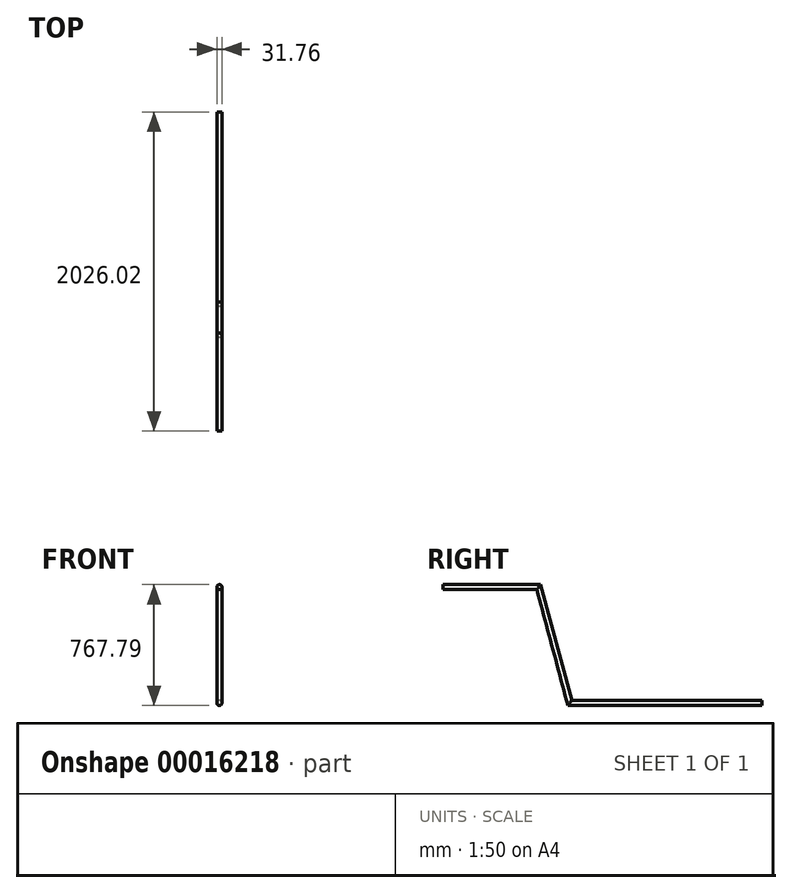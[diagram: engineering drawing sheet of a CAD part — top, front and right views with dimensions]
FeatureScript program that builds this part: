
annotation { "Feature Type Name" : "Feature", "Feature Type Description" : "" }
export const myFeature = defineFeature(function(context is Context, id is Id, definition is map)
    precondition{}
    {
        {
            var Q0;
            Q0=qCreatedBy(makeId("Right.planeOp"),FACE);
            var sketch = newSketch(context, id + "F0", { "sketchPlane" : qUnion([Q0])});
            skLineSegment(sketch, "E0", {"start": v(0, 0) * mm, "end": v(-1219.2, 0) * mm});
            skLineSegment(sketch, "E1", {"start": v(-1219.2, 0) * mm, "end": v(-1416.42, 736.04) * mm});
            skLineSegment(sketch, "E2", {"start": v(-1416.42, 736.04) * mm, "end": v(-2026.02, 736.04) * mm});
            skLineSegment(sketch, "E3", {"start": v(0, 0) * mm, "end": v(-2540, 0) * mm, "construction": true});
            skSolve(sketch);
        }
        {
            var Q0;
            Q0=qCreatedBy(makeId("Front.planeOp"),FACE);
            var sketch = newSketch(context, id + "F1", { "sketchPlane" : qUnion([Q0])});
            skCircle(sketch, "E4", {"center": v(0, 0) * mm, "radius": 15.88 * mm});
            skSolve(sketch);
        }
        {
            var Q0;
            Q0=makeQuery(id+"F1.imprint","IMPRINT",FACE,{"disambiguationData":[TD([[makeQuery(id+"F1.imprint","IMPRINT",EDGE,{"derivedFrom":sQuery(id+"F1.wireOp",EDGE,"E4")}),1.0]])]});
            var Q1;
            Q1=sQuery(id+"F0.wireOp",EDGE,"E0");
            var Q2;
            Q2=sQuery(id+"F0.wireOp",EDGE,"E1");
            var Q3;
            Q3=sQuery(id+"F0.wireOp",EDGE,"E2");
            sweep(context, id + "F2", {"profiles" : qUnion([Q0]), "path" : qUnion([Q1, Q2, Q3])});
        }
    });
